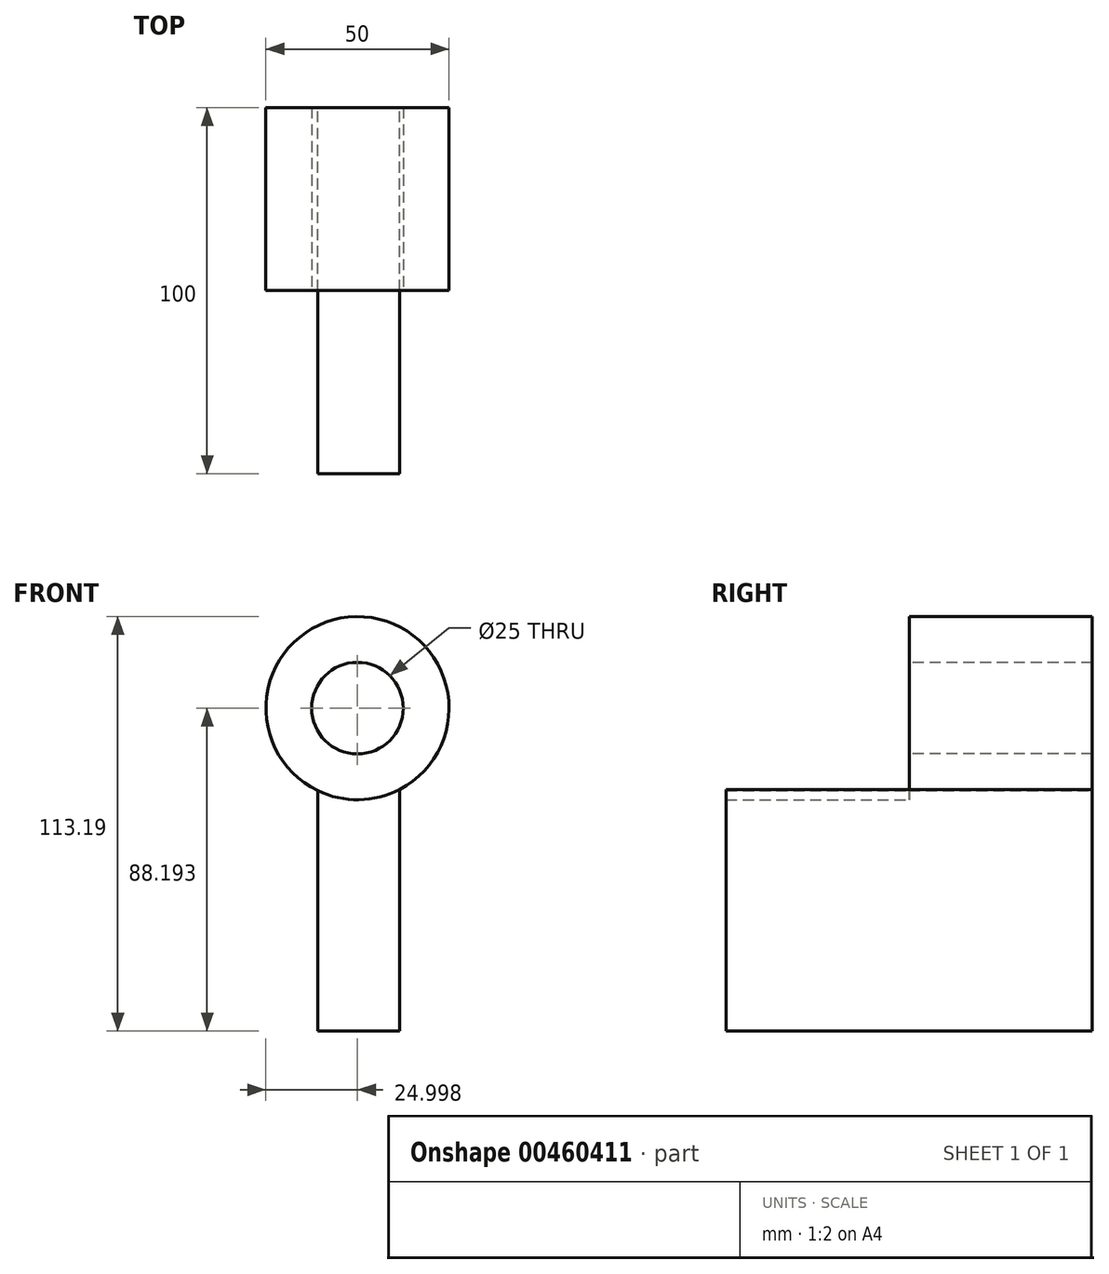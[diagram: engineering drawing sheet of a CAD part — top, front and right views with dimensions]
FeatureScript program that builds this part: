
annotation { "Feature Type Name" : "Feature", "Feature Type Description" : "" }
export const myFeature = defineFeature(function(context is Context, id is Id, definition is map)
    precondition{}
    {
        {
            var Q0;
            Q0=qCreatedBy(makeId("Front.planeOp"),FACE);
            var sketch = newSketch(context, id + "F0", { "sketchPlane" : qUnion([Q0])});
            skCircle(sketch, "E0", {"center": v(-38.34, 39.54) * mm, "radius": 25 * mm});
            skLineSegment(sketch, "E1", {"start": v(-49.15, 17) * mm, "end": v(-49.15, -48.65) * mm});
            skLineSegment(sketch, "E2", {"start": v(-49.15, -48.65) * mm, "end": v(-26.84, -48.65) * mm});
            skLineSegment(sketch, "E3", {"start": v(-26.84, -48.65) * mm, "end": v(-26.84, 17.35) * mm});
            skSolve(sketch);
        }
        {
            var Q0;
            {var subQ0=sQuery(id+"F0.wireOp",EDGE,"E0");var subQ1=makeQuery(id+"F0.imprint","INTERSECT",VERTEX,{"derivedFrom":[subQ0,sQuery(id+"F0.wireOp",EDGE,"E1")]});Q0=makeQuery(id+"F0.imprint","IMPRINT",FACE,{"disambiguationData":[TD([[makeQuery(id+"F0.imprint","IMPRINT",EDGE,{"disambiguationData":[TD([[subQ1,-1.0]])],"derivedFrom":subQ0}),1.0]])]});}
            extrude(context, id + "F1", {"entities" : qUnion([Q0]), "depth" : 50 * mm});
        }
        {
            var Q0;
            {var subQ0=sQuery(id+"F0.wireOp",EDGE,"E1");Q0=makeQuery(id+"F0.imprint","IMPRINT",FACE,{"disambiguationData":[TD([[makeQuery(id+"F0.imprint","IMPRINT",EDGE,{"derivedFrom":subQ0}),1.0]])]});}
            extrude(context, id + "F2", {"entities" : qUnion([Q0]), "operationType" : NewBodyOperationType.ADD, "depth" : 100 * mm});
        }
        {
            var Q0;
            Q0=makeQuery(id+"F1.opExtrude","CAP_FACE",FACE,{"disambiguationData":[OSD([sQuery(id+"F0.wireOp",EDGE,"E0")])],"isStart":false});
            var sketch = newSketch(context, id + "F3", { "sketchPlane" : qUnion([Q0])});
            skCircle(sketch, "E4", {"center": v(-38.34, 39.54) * mm, "radius": 12.5 * mm});
            skSolve(sketch);
        }
        {
            var Q0;
            Q0=makeQuery(id+"F3.imprint","IMPRINT",FACE,{"disambiguationData":[TD([[makeQuery(id+"F3.imprint","IMPRINT",EDGE,{"derivedFrom":sQuery(id+"F3.wireOp",EDGE,"E4")}),1.0]])]});
            var Q1;
            Q1=sQuery(id+"F3.wireOp",EDGE,"E4");
            extrude(context, id + "F4", {"entities" : qUnion([Q0]), "operationType" : NewBodyOperationType.REMOVE, "surfaceEntities" : qUnion([Q1]), "oppositeDirection" : true, "depth" : 50 * mm});
        }
    });
